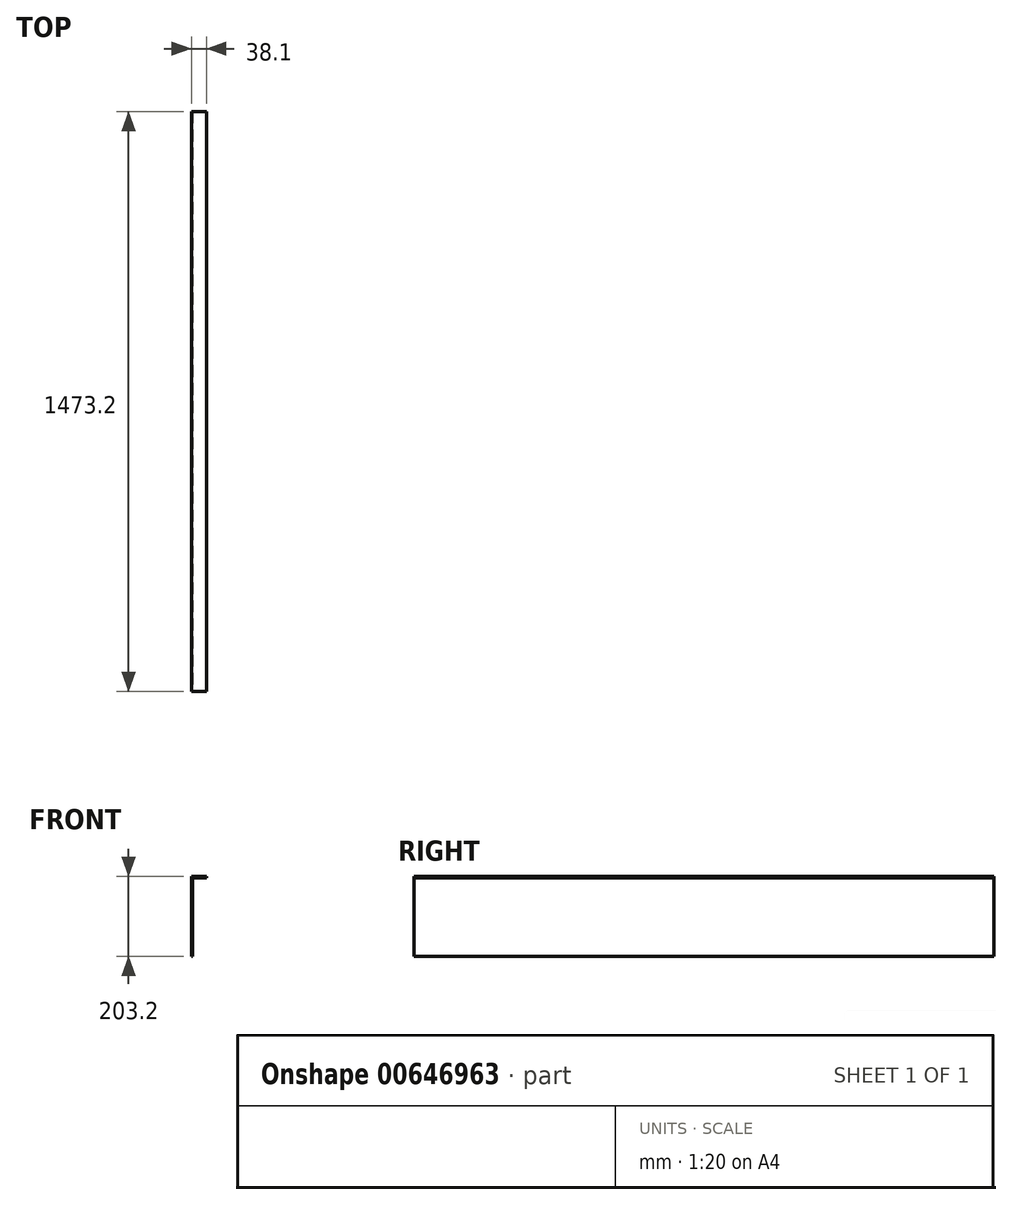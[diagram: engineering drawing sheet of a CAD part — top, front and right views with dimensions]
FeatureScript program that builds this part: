
annotation { "Feature Type Name" : "Feature", "Feature Type Description" : "" }
export const myFeature = defineFeature(function(context is Context, id is Id, definition is map)
    precondition{}
    {
        {
            var Q0;
            Q0=qCreatedBy(makeId("Front.planeOp"),FACE);
            var sketch = newSketch(context, id + "F0", { "sketchPlane" : qUnion([Q0])});
            skLineSegment(sketch, "E0", {"start": v(7.5, 84.6) * mm, "end": v(-30.6, 84.6) * mm});
            skLineSegment(sketch, "E1", {"start": v(-30.6, 84.6) * mm, "end": v(-30.6, -118.6) * mm});
            skLineSegment(sketch, "E2", {"start": v(-30.6, -118.6) * mm, "end": v(-27.43, -118.6) * mm});
            skLineSegment(sketch, "E3", {"start": v(-27.43, -118.6) * mm, "end": v(-27.43, 81.42) * mm});
            skLineSegment(sketch, "E4", {"start": v(-27.43, 81.42) * mm, "end": v(7.5, 81.42) * mm});
            skLineSegment(sketch, "E5", {"start": v(7.5, 81.42) * mm, "end": v(7.5, 84.6) * mm});
            skSolve(sketch);
        }
        {
            var Q0;
            Q0 = qSketchRegion(id + "F0", true);
            extrude(context, id + "F1", {"entities" : qUnion([Q0]), "oppositeDirection" : true, "depth" : 1473.2 * mm, "offsetDistance" : 25.4 * mm});
        }
    });
